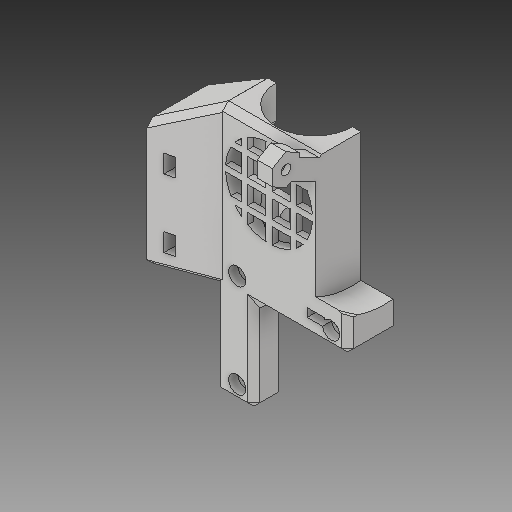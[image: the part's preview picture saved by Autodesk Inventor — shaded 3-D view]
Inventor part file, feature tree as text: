
AUTODESK INVENTOR PART (.ipt)
format: ipt  version: 2018 (Build 220112000, 112)  size: 318,976 bytes
history: native  units: mm
features: other x2, extrude x1
ambient origin geometry x8: Origin, YZ Plane, XZ Plane, XY Plane, X Axis, Y Axis, Z Axis, Center Point
bodies: Solid1 (feature_tree)
feature tree (3):
  extrude  "Extruder Body.ipt"  Depth=10.0mm
  other  "Solid2::Extruder Body.ipt"
  other  "TaggingFeature1"
